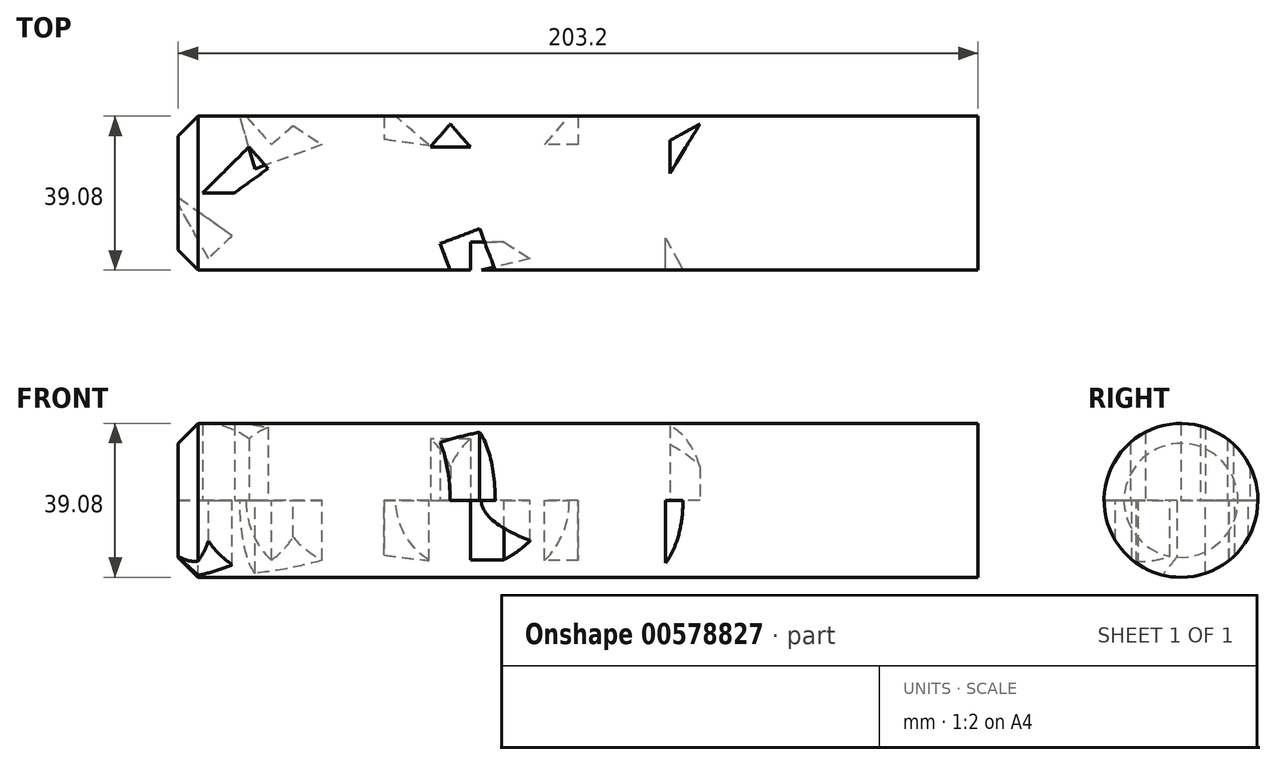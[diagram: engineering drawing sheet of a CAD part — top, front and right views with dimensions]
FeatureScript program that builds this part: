
annotation { "Feature Type Name" : "Feature", "Feature Type Description" : "" }
export const myFeature = defineFeature(function(context is Context, id is Id, definition is map)
    precondition{}
    {
        {
            var Q0;
            Q0=qCreatedBy(makeId("Right.planeOp"),FACE);
            var sketch = newSketch(context, id + "F0", { "sketchPlane" : qUnion([Q0])});
            skCircle(sketch, "E0", {"center": v(0, 0) * mm, "radius": 19.54 * mm});
            skSolve(sketch);
        }
        {
            var Q0;
            Q0 = qSketchRegion(id + "F0", true);
            extrude(context, id + "F1", {"entities" : qUnion([Q0]), "endBound" : BoundingType.SYMMETRIC, "depth" : 203.2 * mm, "offsetDistance" : 25.4 * mm});
        }
        {
            var Q0;
            Q0=qCreatedBy(makeId("Top.planeOp"),FACE);
            var sketch = newSketch(context, id + "F2", { "sketchPlane" : qUnion([Q0])});
            skLineSegment(sketch, "E1", {"start": v(-37.93, 12.17) * mm, "end": v(-49.35, 22.17) * mm});
            skLineSegment(sketch, "E2", {"start": v(-49.35, 22.17) * mm, "end": v(-49.35, 13.74) * mm});
            skLineSegment(sketch, "E3", {"start": v(-49.35, 13.74) * mm, "end": v(-37.93, 12.17) * mm});
            skSolve(sketch);
        }
        {
            var Q0;
            Q0 = qSketchRegion(id + "F2", true);
            extrude(context, id + "F3", {"entities" : qUnion([Q0]), "operationType" : NewBodyOperationType.REMOVE, "oppositeDirection" : true, "depth" : 38.1 * mm, "offsetDistance" : 25.4 * mm});
        }
        {
            var Q0;
            Q0=qCreatedBy(makeId("Top.planeOp"),FACE);
            var sketch = newSketch(context, id + "F4", { "sketchPlane" : qUnion([Q0])});
            skLineSegment(sketch, "E4", {"start": v(-93.94, -16.62) * mm, "end": v(-103.17, 0) * mm});
            skLineSegment(sketch, "E5", {"start": v(-103.17, 0) * mm, "end": v(-87.87, -10.76) * mm});
            skLineSegment(sketch, "E6", {"start": v(-87.87, -10.76) * mm, "end": v(-93.94, -16.62) * mm});
            skLineSegment(sketch, "E7", {"start": v(22.21, -20.18) * mm, "end": v(22.21, -11.35) * mm});
            skLineSegment(sketch, "E8", {"start": v(22.21, -11.35) * mm, "end": v(26.97, -20.18) * mm});
            skLineSegment(sketch, "E9", {"start": v(26.97, -20.18) * mm, "end": v(22.21, -20.18) * mm});
            skLineSegment(sketch, "E10", {"start": v(-86.71, 22.14) * mm, "end": v(-77.96, 12.29) * mm});
            skLineSegment(sketch, "E11", {"start": v(-77.96, 12.29) * mm, "end": v(-72.45, 17.18) * mm});
            skLineSegment(sketch, "E12", {"start": v(-72.45, 17.18) * mm, "end": v(-65.02, 12.29) * mm});
            skLineSegment(sketch, "E13", {"start": v(-65.02, 12.29) * mm, "end": v(-82.07, 6.16) * mm});
            skLineSegment(sketch, "E14", {"start": v(-82.07, 6.16) * mm, "end": v(-86.71, 22.14) * mm});
            skLineSegment(sketch, "E15", {"start": v(-8.54, 12.29) * mm, "end": v(0, 22.14) * mm});
            skLineSegment(sketch, "E16", {"start": v(0, 22.14) * mm, "end": v(0, 12.29) * mm});
            skLineSegment(sketch, "E17", {"start": v(0, 12.29) * mm, "end": v(-8.54, 12.29) * mm});
            skLineSegment(sketch, "E18", {"start": v(-27.37, -20.18) * mm, "end": v(-27.37, -12.42) * mm});
            skLineSegment(sketch, "E19", {"start": v(-27.37, -12.42) * mm, "end": v(-18.88, -12.42) * mm});
            skLineSegment(sketch, "E20", {"start": v(-18.88, -12.42) * mm, "end": v(-12.21, -16.67) * mm});
            skLineSegment(sketch, "E21", {"start": v(-12.21, -16.67) * mm, "end": v(-27.37, -20.18) * mm});
            skSolve(sketch);
        }
        {
            var Q0;
            Q0 = qSketchRegion(id + "F4", true);
            extrude(context, id + "F5", {"entities" : qUnion([Q0]), "operationType" : NewBodyOperationType.REMOVE, "oppositeDirection" : true, "depth" : 25.4 * mm, "offsetDistance" : 25.4 * mm});
        }
        {
            var Q0;
            Q0=qCreatedBy(makeId("Top.planeOp"),FACE);
            var sketch = newSketch(context, id + "F6", { "sketchPlane" : qUnion([Q0])});
            skLineSegment(sketch, "E22", {"start": v(-20.06, -22.16) * mm, "end": v(-25.06, -9.04) * mm});
            skLineSegment(sketch, "E23", {"start": v(-25.06, -9.04) * mm, "end": v(-35.09, -12.85) * mm});
            skLineSegment(sketch, "E24", {"start": v(-35.09, -12.85) * mm, "end": v(-32.05, -20.82) * mm});
            skLineSegment(sketch, "E25", {"start": v(-32.05, -20.82) * mm, "end": v(-20.06, -22.16) * mm});
            skLineSegment(sketch, "E26", {"start": v(30.9, 17.55) * mm, "end": v(23.29, 4.98) * mm});
            skLineSegment(sketch, "E27", {"start": v(23.29, 4.98) * mm, "end": v(23.29, 13.33) * mm});
            skLineSegment(sketch, "E28", {"start": v(23.29, 13.33) * mm, "end": v(30.9, 17.55) * mm});
            skLineSegment(sketch, "E29", {"start": v(-83.62, 11.74) * mm, "end": v(-95.48, 0) * mm});
            skLineSegment(sketch, "E30", {"start": v(-95.48, 0) * mm, "end": v(-87.36, 0) * mm});
            skLineSegment(sketch, "E31", {"start": v(-87.36, 0) * mm, "end": v(-78.82, 6.23) * mm});
            skLineSegment(sketch, "E32", {"start": v(-78.82, 6.23) * mm, "end": v(-83.62, 11.74) * mm});
            skLineSegment(sketch, "E33", {"start": v(-100.13, 11.74) * mm, "end": v(-103.42, 0) * mm});
            skLineSegment(sketch, "E34", {"start": v(-103.42, 0) * mm, "end": v(-100.13, 11.74) * mm});
            skLineSegment(sketch, "E35", {"start": v(-37.57, 11.74) * mm, "end": v(-27.4, 11.74) * mm});
            skLineSegment(sketch, "E36", {"start": v(-27.4, 11.74) * mm, "end": v(-32.48, 17.55) * mm});
            skPoint(sketch, "E36.endSnap0", {"position": v(-32.48, 11.74) * mm});
            skLineSegment(sketch, "E37", {"start": v(-32.48, 17.55) * mm, "end": v(-37.57, 11.74) * mm});
            skSolve(sketch);
        }
        {
            var Q0;
            Q0 = qSketchRegion(id + "F6", true);
            extrude(context, id + "F7", {"entities" : qUnion([Q0]), "operationType" : NewBodyOperationType.REMOVE, "depth" : 25.4 * mm, "offsetDistance" : 25.4 * mm});
        }
        {
            var Q0;
            Q0=makeQuery(id+"F1.opExtrude","CAP_EDGE",EDGE,{"disambiguationData":[OSD([sQuery(id+"F0.wireOp",EDGE,"E0")])],"isStart":true});
            chamfer(context, id + "F8", {"entities" : qUnion([Q0]), "width" : 5.08 * mm, "tangentPropagation" : true});
        }
    });
